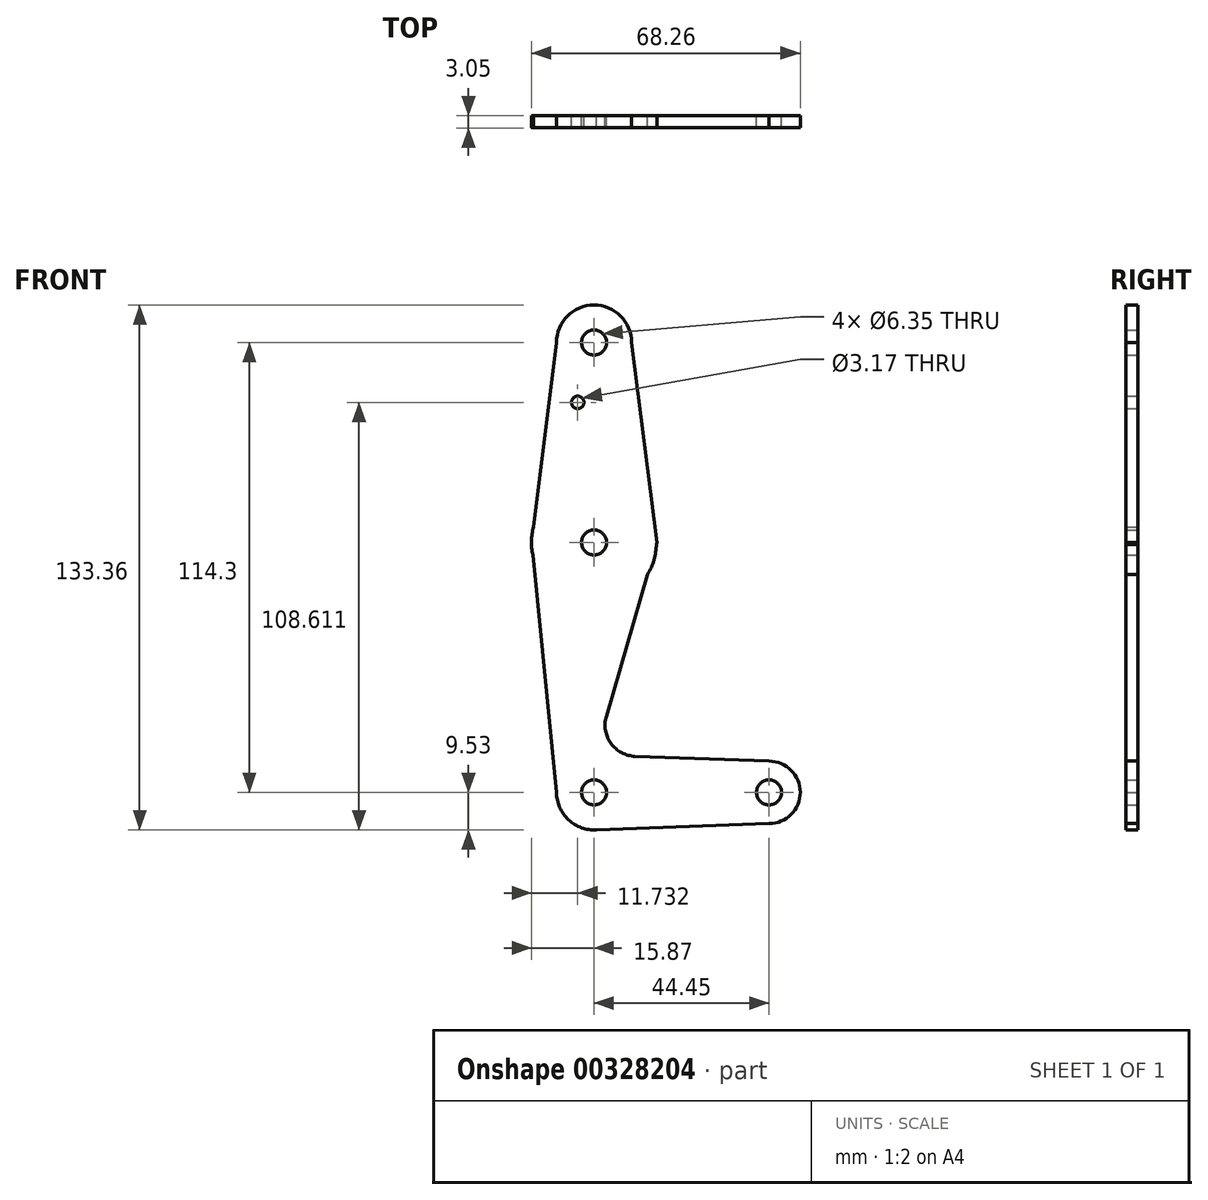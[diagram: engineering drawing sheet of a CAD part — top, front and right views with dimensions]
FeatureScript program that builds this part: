
annotation { "Feature Type Name" : "Feature", "Feature Type Description" : "" }
export const myFeature = defineFeature(function(context is Context, id is Id, definition is map)
    precondition{}
    {
        {
            var Q0;
            Q0=qCreatedBy(makeId("Front.planeOp"),FACE);
            var sketch = newSketch(context, id + "F0", { "sketchPlane" : qUnion([Q0])});
            skLineSegment(sketch, "E0", {"start": v(0, 0) * mm, "end": v(0, 114.3) * mm, "construction": true});
            skCircle(sketch, "E1", {"center": v(0, 114.3) * mm, "radius": 9.53 * mm});
            skCircle(sketch, "E2", {"center": v(0, 0) * mm, "radius": 9.53 * mm});
            skLineSegment(sketch, "E3", {"start": v(0, 0) * mm, "end": v(44.45, 0) * mm, "construction": true});
            skCircle(sketch, "E4", {"center": v(44.45, 0) * mm, "radius": 7.94 * mm});
            skCircle(sketch, "E5", {"center": v(0, 63.5) * mm, "radius": 15.88 * mm});
            skLineSegment(sketch, "E6", {"start": v(9.53, 114.3) * mm, "end": v(16, 63.5) * mm});
            skLineSegment(sketch, "E7", {"start": v(-9.53, 114.3) * mm, "end": v(-15.88, 63.5) * mm});
            skLineSegment(sketch, "E8", {"start": v(-15.88, 63.5) * mm, "end": v(-9.53, 0) * mm});
            skLineSegment(sketch, "E9", {"start": v(16, 63.5) * mm, "end": v(3.11, 19.32) * mm});
            skLineSegment(sketch, "E10", {"start": v(10.46, 9.15) * mm, "end": v(44.45, 7.94) * mm});
            skLineSegment(sketch, "E11", {"start": v(44.45, -7.94) * mm, "end": v(0, -9.52) * mm});
            skCircle(sketch, "E12", {"center": v(-4.14, 99.08) * mm, "radius": 1.59 * mm});
            skCircle(sketch, "E13", {"center": v(0, 114.3) * mm, "radius": 3.18 * mm});
            skCircle(sketch, "E14", {"center": v(0, 63.5) * mm, "radius": 3.18 * mm});
            skCircle(sketch, "E15", {"center": v(0, 0) * mm, "radius": 3.18 * mm});
            skCircle(sketch, "E16", {"center": v(44.45, 0) * mm, "radius": 3.18 * mm});
            skArc(sketch, "E17.filletArc", {"start": v(3.11, 19.32) * mm, "mid": v(4.3, 12.44) * mm, "end": v(10.46, 9.15) * mm});
            skSolve(sketch);
        }
        {
            var Q0;
            Q0 = qSketchRegion(id + "F0", true);
            extrude(context, id + "F1", {"entities" : qUnion([Q0]), "depth" : 3.05 * mm});
        }
    });
